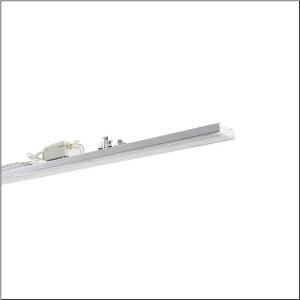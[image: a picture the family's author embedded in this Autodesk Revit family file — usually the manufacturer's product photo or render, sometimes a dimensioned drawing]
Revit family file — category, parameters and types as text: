
# Revit family: licross_r__21_recessed_ho_52te11dn4e5s_c18d
name_source: partatom
category: Lighting Fixtures
units: mm (PartAtom-declared; Revit-internal decimal feet)

## family parameters
Cut with Voids When Loaded = No
Host = Face
Light Source = No
Part Type = Normal
Room Calculation Point = No
Round Connector Dimension = Use Diameter
Shared = No

## types (1)
- --- (1 x LED, 14970 lm, 84.6 W, 4000K)
    Apparent Load = 85 VA
    CIE Flux Codes = 87 95 99 100 100
    Color Rendering = 80
    Color Temperature = 4000K
    Default Elevation = 1800 mm
    Description = Licross® 21 Recessed HO, luminaire insert, of sheet steel, galvanised, coil coated, white, length: 1.500mm, width: 66mm, height: 67mm, LED rated luminous flux: 14.970lm, light colour: 840, control gear: DALI 2, with plug, 5-pole, with phase selection, mains connection: 220..240V, AC, 50/60Hz, rated input power: 85W, halogen-free wiring, primary light control with lens, of plastic, primary optical cover: cover, of PMMA, light emission: direct distribution, primary light characteristic: symmetric, protection rating (complete): IP54, insulation class (complete): insulation class I (protective earthing), certification: CE, ENEC, VDE, UKCA, protection symbol: D if used in an environment with non-conductive dust loads with corresponding accessories, impact resistance: IK06, permissible ambient temperature for indoor applications: -25..+30°C, corresponds to IFS (International Featured Standards) requirements for safety and quality in the food industry, reducing of maximum allowable ambient temperature of 5°C with ceiling mounting, LABS conformity tested according to VDMA 24364:2018-05, packaging unit: 1 piece
    Height = 58 mm
    Lamp = 1 x LED
    Lamp Light Flux = 14970 lm
    Lamp Power = 84.6 W
    Lamp count = 1
    Length = 1500 mm
    Luminous efficacy = 177 lm/W
    Manufacturer = Siteco
    ModVariant = No
    Model = 52TE11DN4E5S
    Mounting Place = Ceiling
    Mounting Type = Pendant
    Number of Poles = 1
    OnlyDefault = Yes
    Power Factor = 1
    Product Name = Licross® 21 Recessed HO
    Product group = luminaire insert
    ProductGroupID = 901
    Protection Class = Protection class I
    Protection Degree = IP 54
    RLX_Detail_Level = 1
    RLX_Emergency_Light_Flux = 0 lm
    RLX_Emergency_Type = 0
    RLX_Emergency_Type_DB = No
    RlxData = <blob elided: 24593 chars, md5=a187fe7e>
    Socket = socket
    Standby Power = 0 W
    System Light Flux = 14970 lm
    System Power = 85 W
    Type Comments = factory setting: luminous flux: 100 % | dim-lin: 254 | 484 mA
    Type Image = l_1296930.jpg
    URL = http://relux.com
    VarID = @adj_058781
    Voltage = 0 V
    Weight = 0.00 kg
    Width = 66 mm

## geometry (parser evidence)
native form markers: Blend x4, Sweep x12
no freeform markers — native parametric forms only
